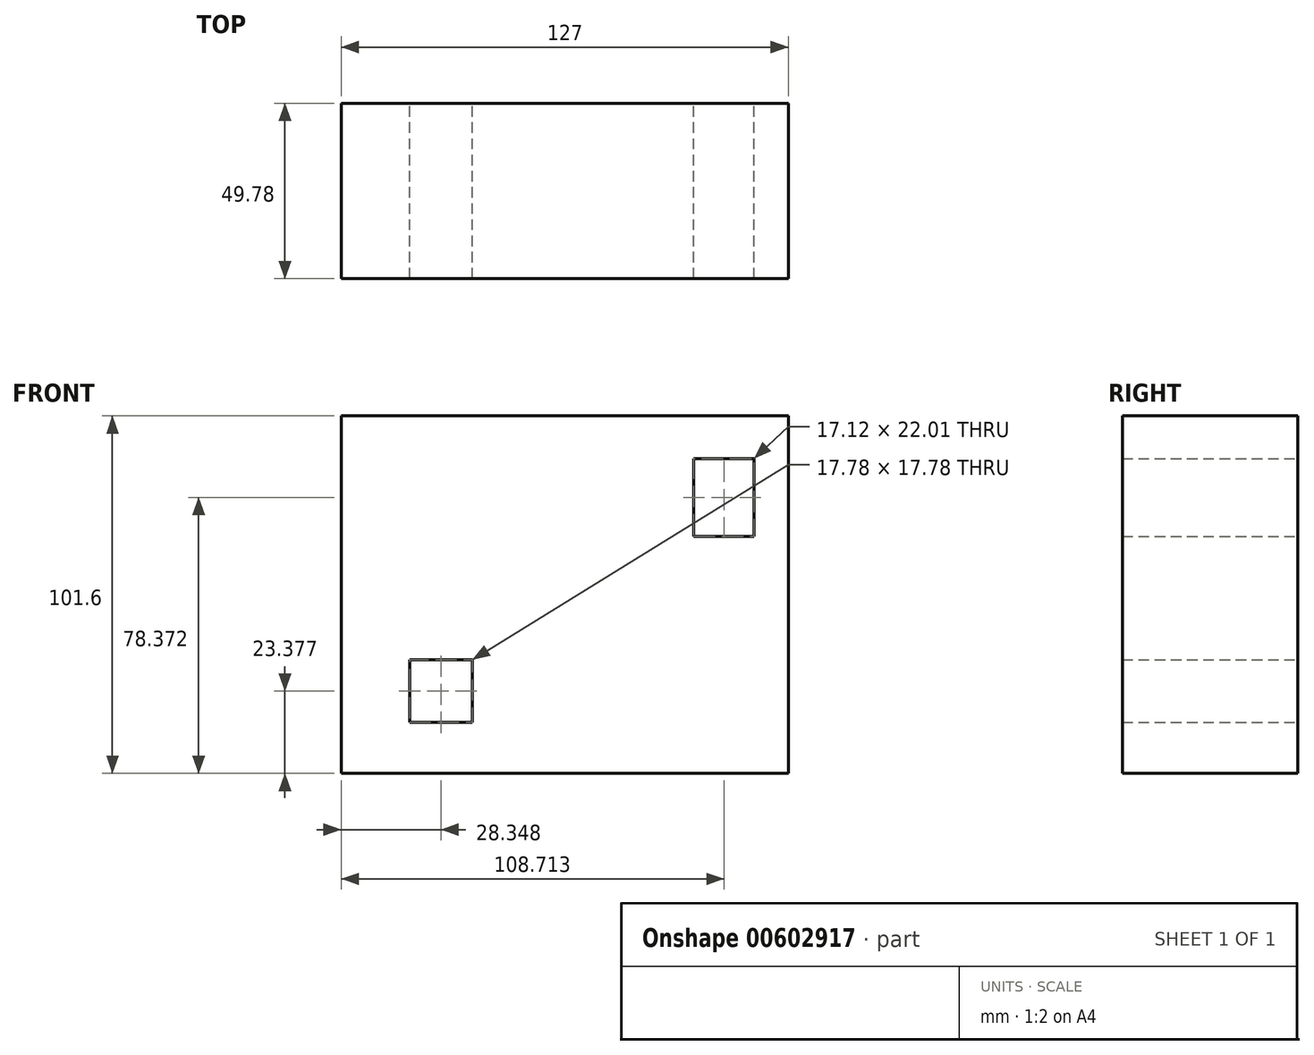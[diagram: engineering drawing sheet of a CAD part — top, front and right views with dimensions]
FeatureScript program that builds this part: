
annotation { "Feature Type Name" : "Feature", "Feature Type Description" : "" }
export const myFeature = defineFeature(function(context is Context, id is Id, definition is map)
    precondition{}
    {
        {
            var Q0;
            Q0=qCreatedBy(makeId("Front.planeOp"),FACE);
            var sketch = newSketch(context, id + "F0", { "sketchPlane" : qUnion([Q0])});
            skLineSegment(sketch, "E0.bottom", {"start": v(-62.75, 50.8) * mm, "end": v(64.25, 50.8) * mm});
            skLineSegment(sketch, "E0.top", {"start": v(-62.75, -50.8) * mm, "end": v(64.25, -50.8) * mm});
            skLineSegment(sketch, "E0.left", {"start": v(-62.75, 50.8) * mm, "end": v(-62.75, -50.8) * mm});
            skLineSegment(sketch, "E0.right", {"start": v(64.25, 50.8) * mm, "end": v(64.25, -50.8) * mm});
            skLineSegment(sketch, "E1.bottom", {"start": v(-43.3, -18.53) * mm, "end": v(-25.51, -18.53) * mm});
            skLineSegment(sketch, "E1.top", {"start": v(-43.3, -36.31) * mm, "end": v(-25.51, -36.31) * mm});
            skLineSegment(sketch, "E1.left", {"start": v(-43.3, -18.53) * mm, "end": v(-43.3, -36.31) * mm});
            skLineSegment(sketch, "E1.right", {"start": v(-25.51, -18.53) * mm, "end": v(-25.51, -36.31) * mm});
            skLineSegment(sketch, "E2.bottom", {"start": v(37.4, 38.58) * mm, "end": v(54.52, 38.58) * mm});
            skLineSegment(sketch, "E2.top", {"start": v(37.4, 16.57) * mm, "end": v(54.52, 16.57) * mm});
            skLineSegment(sketch, "E2.left", {"start": v(37.4, 38.58) * mm, "end": v(37.4, 16.57) * mm});
            skLineSegment(sketch, "E2.right", {"start": v(54.52, 38.58) * mm, "end": v(54.52, 16.57) * mm});
            skSolve(sketch);
        }
        {
            var Q0;
            Q0=makeQuery(id+"F0.imprint","IMPRINT",FACE,{"disambiguationData":[TD([[makeQuery(id+"F0.imprint","IMPRINT",EDGE,{"derivedFrom":sQuery(id+"F0.wireOp",EDGE,"E0.bottom")}),-1.0]])]});
            extrude(context, id + "F1", {"entities" : qUnion([Q0]), "depth" : 49.78 * mm, "offsetDistance" : 25.4 * mm});
        }
    });
